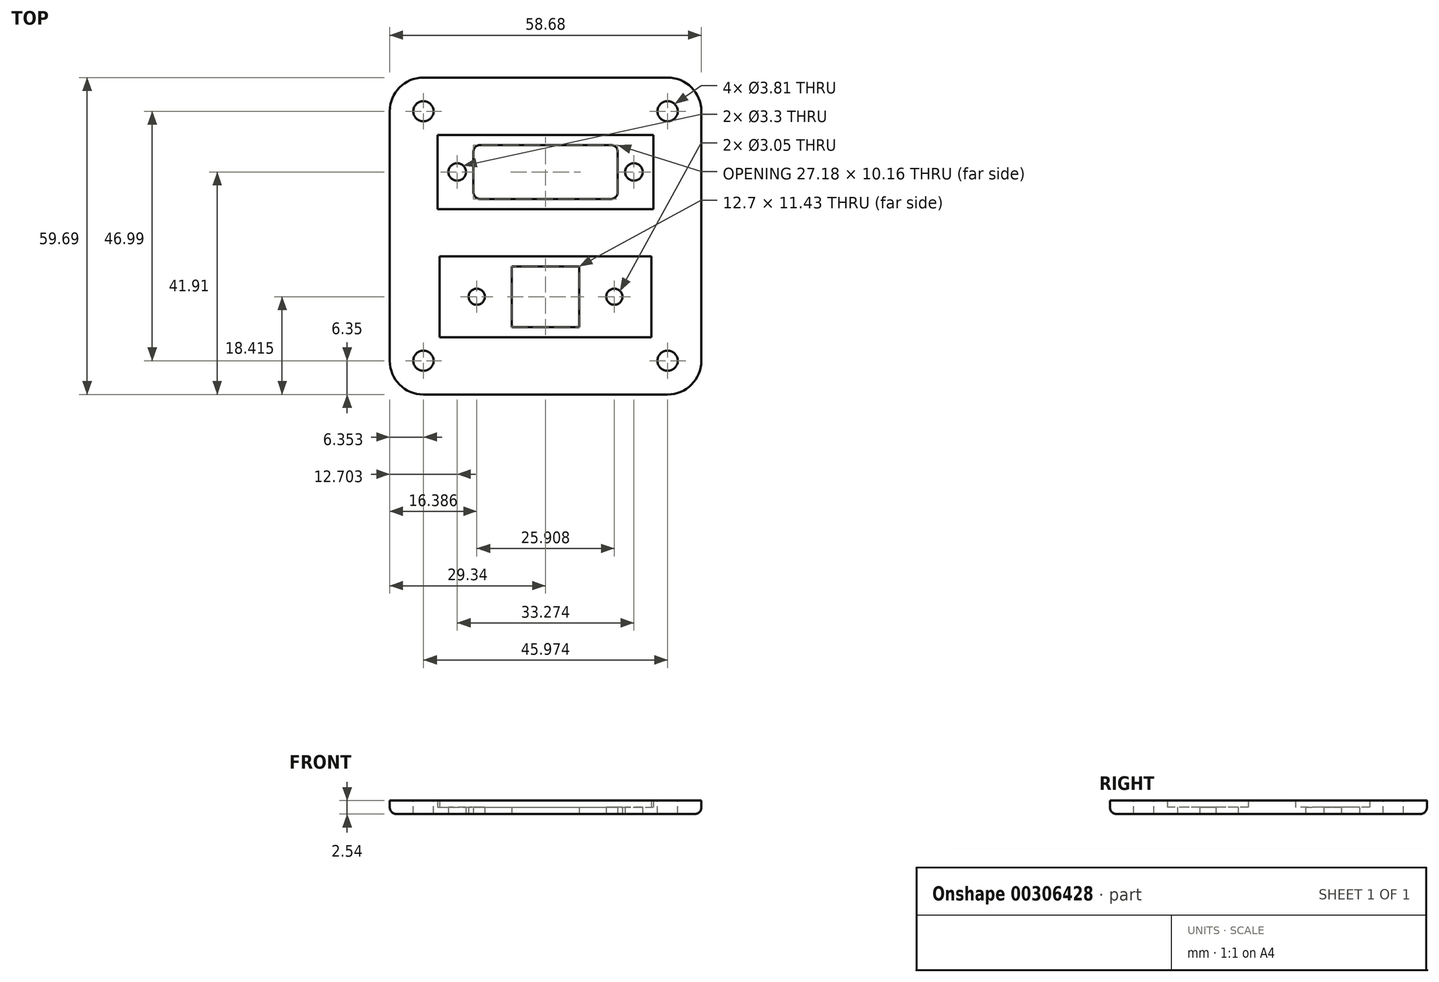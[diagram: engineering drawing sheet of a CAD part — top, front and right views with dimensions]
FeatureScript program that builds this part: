
annotation { "Feature Type Name" : "Feature", "Feature Type Description" : "" }
export const myFeature = defineFeature(function(context is Context, id is Id, definition is map)
    precondition{}
    {
        {
            var Q0;
            Q0=qCreatedBy(makeId("Top.planeOp"),FACE);
            var sketch = newSketch(context, id + "F0", { "sketchPlane" : qUnion([Q0])});
            skCircle(sketch, "E0", {"center": v(-16.64, 0) * mm, "radius": 1.65 * mm});
            skCircle(sketch, "E1", {"center": v(16.64, 0) * mm, "radius": 1.65 * mm});
            skLineSegment(sketch, "E2", {"start": v(-16.64, 0) * mm, "end": v(16.64, 0) * mm, "construction": true});
            skPoint(sketch, "E3", {"position": v(0, 0) * mm});
            skLineSegment(sketch, "E4.bottom", {"start": v(-13.59, 5.08) * mm, "end": v(13.59, 5.08) * mm});
            skLineSegment(sketch, "E4.top", {"start": v(-13.59, -5.08) * mm, "end": v(13.59, -5.08) * mm});
            skLineSegment(sketch, "E4.left", {"start": v(-13.59, 5.08) * mm, "end": v(-13.59, -5.08) * mm});
            skLineSegment(sketch, "E4.right", {"start": v(13.59, 5.08) * mm, "end": v(13.59, -5.08) * mm});
            skLineSegment(sketch, "E5.bottom", {"start": v(-6.35, -17.78) * mm, "end": v(6.35, -17.78) * mm});
            skLineSegment(sketch, "E5.top", {"start": v(-6.35, -29.21) * mm, "end": v(6.35, -29.21) * mm});
            skLineSegment(sketch, "E5.left", {"start": v(-6.35, -17.78) * mm, "end": v(-6.35, -29.21) * mm});
            skLineSegment(sketch, "E5.right", {"start": v(6.35, -17.78) * mm, "end": v(6.35, -29.21) * mm});
            skPoint(sketch, "E5.middle", {"position": v(0, -23.5) * mm});
            skCircle(sketch, "E6", {"center": v(-12.95, -23.5) * mm, "radius": 1.52 * mm});
            skCircle(sketch, "E7", {"center": v(12.95, -23.5) * mm, "radius": 1.52 * mm});
            skLineSegment(sketch, "E8", {"start": v(-12.95, -23.5) * mm, "end": v(12.95, -23.5) * mm, "construction": true});
            skLineSegment(sketch, "E9.bottom", {"start": v(-29.34, 17.78) * mm, "end": v(29.34, 17.78) * mm});
            skLineSegment(sketch, "E9.top", {"start": v(-29.34, -41.91) * mm, "end": v(29.34, -41.91) * mm});
            skLineSegment(sketch, "E9.left", {"start": v(-29.34, 17.78) * mm, "end": v(-29.34, -41.91) * mm});
            skLineSegment(sketch, "E9.right", {"start": v(29.34, 17.78) * mm, "end": v(29.34, -41.9) * mm});
            skLineSegment(sketch, "E10", {"start": v(-13.59, 5.08) * mm, "end": v(-13.59, 17.78) * mm, "construction": true});
            skLineSegment(sketch, "E11", {"start": v(6.35, -29.21) * mm, "end": v(6.35, -41.91) * mm, "construction": true});
            skLineSegment(sketch, "E12", {"start": v(-16.64, 0) * mm, "end": v(-29.34, 0) * mm, "construction": true});
            skPoint(sketch, "E13", {"position": v(0, 17.78) * mm});
            skSolve(sketch);
        }
        {
            var Q0;
            Q0 = qSketchRegion(id + "F0", true);
            extrude(context, id + "F1", {"entities" : qUnion([Q0]), "depth" : 1.27 * mm});
        }
        {
            var Q0;
            Q0=makeQuery(id+"F1.opExtrude","CAP_FACE",FACE,{"disambiguationData":[OSD([sQuery(id+"F0.wireOp",EDGE,"E0"),sQuery(id+"F0.wireOp",EDGE,"E1"),sQuery(id+"F0.wireOp",EDGE,"E4.bottom"),sQuery(id+"F0.wireOp",EDGE,"E4.top"),sQuery(id+"F0.wireOp",EDGE,"E4.left"),sQuery(id+"F0.wireOp",EDGE,"E4.right"),sQuery(id+"F0.wireOp",EDGE,"E5.bottom"),sQuery(id+"F0.wireOp",EDGE,"E5.top"),sQuery(id+"F0.wireOp",EDGE,"E5.left"),sQuery(id+"F0.wireOp",EDGE,"E5.right"),sQuery(id+"F0.wireOp",EDGE,"E6"),sQuery(id+"F0.wireOp",EDGE,"E7"),sQuery(id+"F0.wireOp",EDGE,"E9.bottom"),sQuery(id+"F0.wireOp",EDGE,"E9.top"),sQuery(id+"F0.wireOp",EDGE,"E9.left"),sQuery(id+"F0.wireOp",EDGE,"E9.right")])],"isStart":false});
            var sketch = newSketch(context, id + "F2", { "sketchPlane" : qUnion([Q0])});
            skLineSegment(sketch, "E14.bottom", {"start": v(-20.32, 6.99) * mm, "end": v(20.32, 6.99) * mm});
            skLineSegment(sketch, "E14.top", {"start": v(-20.32, -6.99) * mm, "end": v(20.32, -6.99) * mm});
            skLineSegment(sketch, "E14.left", {"start": v(-20.32, 6.99) * mm, "end": v(-20.32, -6.99) * mm});
            skLineSegment(sketch, "E14.right", {"start": v(20.32, 6.99) * mm, "end": v(20.32, -6.99) * mm});
            skPoint(sketch, "E14.middle", {"position": v(0, 0) * mm});
            skLineSegment(sketch, "E15.bottom", {"start": v(-29.34, 17.78) * mm, "end": v(29.34, 17.78) * mm});
            skLineSegment(sketch, "E15.top", {"start": v(-29.34, -41.9) * mm, "end": v(29.34, -41.9) * mm});
            skLineSegment(sketch, "E15.left", {"start": v(-29.34, 17.78) * mm, "end": v(-29.34, -41.91) * mm});
            skLineSegment(sketch, "E15.right", {"start": v(29.34, 17.78) * mm, "end": v(29.34, -41.9) * mm});
            skLineSegment(sketch, "E16.bottom", {"start": v(-19.94, -15.88) * mm, "end": v(19.94, -15.88) * mm});
            skLineSegment(sketch, "E16.top", {"start": v(-19.94, -31.12) * mm, "end": v(19.94, -31.12) * mm});
            skLineSegment(sketch, "E16.left", {"start": v(-19.94, -15.88) * mm, "end": v(-19.94, -31.12) * mm});
            skLineSegment(sketch, "E16.right", {"start": v(19.94, -15.88) * mm, "end": v(19.94, -31.12) * mm});
            skPoint(sketch, "E16.middle", {"position": v(0, -23.5) * mm});
            skPoint(sketch, "E16.middle.positionSnap0", {"position": v(0, -29.21) * mm});
            skPoint(sketch, "E16.centerSnap0", {"position": v(0, -29.21) * mm});
            skSolve(sketch);
        }
        {
            var Q0;
            Q0 = qSketchRegion(id + "F2", true);
            extrude(context, id + "F3", {"entities" : qUnion([Q0]), "operationType" : NewBodyOperationType.ADD, "depth" : 1.27 * mm});
        }
        {
            var Q0;
            Q0=makeQuery(id+"F3.boolean.opBoolean","MERGE",EDGE,{"derivedFrom":[makeQuery(id+"F1.opExtrude","SWEPT_EDGE",EDGE,{"disambiguationData":[OSD([sQuery(id+"F0.wireOp",EDGE,"E9.top"),sQuery(id+"F0.wireOp",EDGE,"E9.left")])]}),makeQuery(id+"F3.opExtrude","SWEPT_EDGE",EDGE,{"disambiguationData":[OSD([sQuery(id+"F2.wireOp",EDGE,"E15.top"),sQuery(id+"F2.wireOp",EDGE,"E15.left")])]})]});
            var Q1;
            Q1=makeQuery(id+"F3.boolean.opBoolean","MERGE",EDGE,{"derivedFrom":[makeQuery(id+"F1.opExtrude","SWEPT_EDGE",EDGE,{"disambiguationData":[OSD([sQuery(id+"F0.wireOp",EDGE,"E9.bottom"),sQuery(id+"F0.wireOp",EDGE,"E9.right")])]}),makeQuery(id+"F3.opExtrude","SWEPT_EDGE",EDGE,{"disambiguationData":[OSD([sQuery(id+"F2.wireOp",EDGE,"E15.bottom"),sQuery(id+"F2.wireOp",EDGE,"E15.right")])]})]});
            var Q2;
            Q2=makeQuery(id+"F3.boolean.opBoolean","MERGE",EDGE,{"derivedFrom":[makeQuery(id+"F1.opExtrude","SWEPT_EDGE",EDGE,{"disambiguationData":[OSD([sQuery(id+"F0.wireOp",EDGE,"E9.top"),sQuery(id+"F0.wireOp",EDGE,"E9.right")])]}),makeQuery(id+"F3.opExtrude","SWEPT_EDGE",EDGE,{"disambiguationData":[OSD([sQuery(id+"F2.wireOp",EDGE,"E15.top"),sQuery(id+"F2.wireOp",EDGE,"E15.right")])]})]});
            var Q3;
            Q3=makeQuery(id+"F3.boolean.opBoolean","MERGE",EDGE,{"derivedFrom":[makeQuery(id+"F1.opExtrude","SWEPT_EDGE",EDGE,{"disambiguationData":[OSD([sQuery(id+"F0.wireOp",EDGE,"E9.bottom"),sQuery(id+"F0.wireOp",EDGE,"E9.left")])]}),makeQuery(id+"F3.opExtrude","SWEPT_EDGE",EDGE,{"disambiguationData":[OSD([sQuery(id+"F2.wireOp",EDGE,"E15.bottom"),sQuery(id+"F2.wireOp",EDGE,"E15.left")])]})]});
            fillet(context, id + "F4", {"entities" : qUnion([Q0, Q1, Q2, Q3]), "radius" : 6.35 * mm, "tangentPropagation" : true, "allowEdgeOverflow" : false});
        }
        {
            var Q0;
            {var subQ0=sQuery(id+"F0.wireOp",EDGE,"E9.left");var subQ1=sQuery(id+"F0.wireOp",EDGE,"E9.top");Q0=makeQuery(id+"F4.opFillet","BLEND_EDGE",EDGE,{"blendedFrom":[makeQuery(id+"F3.boolean.opBoolean","MERGE",EDGE,{"derivedFrom":[makeQuery(id+"F1.opExtrude","SWEPT_EDGE",EDGE,{"disambiguationData":[OSD([subQ1,subQ0])]}),makeQuery(id+"F3.opExtrude","SWEPT_EDGE",EDGE,{"disambiguationData":[OSD([sQuery(id+"F2.wireOp",EDGE,"E15.top"),sQuery(id+"F2.wireOp",EDGE,"E15.left")])]})]}),makeQuery(id+"F1.opExtrude","CAP_FACE",FACE,{"disambiguationData":[OSD([sQuery(id+"F0.wireOp",EDGE,"E0"),sQuery(id+"F0.wireOp",EDGE,"E1"),sQuery(id+"F0.wireOp",EDGE,"E4.bottom"),sQuery(id+"F0.wireOp",EDGE,"E4.top"),sQuery(id+"F0.wireOp",EDGE,"E4.left"),sQuery(id+"F0.wireOp",EDGE,"E4.right"),sQuery(id+"F0.wireOp",EDGE,"E5.bottom"),sQuery(id+"F0.wireOp",EDGE,"E5.top"),sQuery(id+"F0.wireOp",EDGE,"E5.left"),sQuery(id+"F0.wireOp",EDGE,"E5.right"),sQuery(id+"F0.wireOp",EDGE,"E6"),sQuery(id+"F0.wireOp",EDGE,"E7"),sQuery(id+"F0.wireOp",EDGE,"E9.bottom"),subQ1,subQ0,sQuery(id+"F0.wireOp",EDGE,"E9.right")])],"isStart":true})],"blendedInto":[makeQuery(id+"F1.opExtrude","CAP_FACE",FACE,{"disambiguationData":[OSD([sQuery(id+"F0.wireOp",EDGE,"E0"),sQuery(id+"F0.wireOp",EDGE,"E1"),sQuery(id+"F0.wireOp",EDGE,"E4.bottom"),sQuery(id+"F0.wireOp",EDGE,"E4.top"),sQuery(id+"F0.wireOp",EDGE,"E4.left"),sQuery(id+"F0.wireOp",EDGE,"E4.right"),sQuery(id+"F0.wireOp",EDGE,"E5.bottom"),sQuery(id+"F0.wireOp",EDGE,"E5.top"),sQuery(id+"F0.wireOp",EDGE,"E5.left"),sQuery(id+"F0.wireOp",EDGE,"E5.right"),sQuery(id+"F0.wireOp",EDGE,"E6"),sQuery(id+"F0.wireOp",EDGE,"E7"),sQuery(id+"F0.wireOp",EDGE,"E9.bottom"),subQ1,subQ0,sQuery(id+"F0.wireOp",EDGE,"E9.right")])],"isStart":true})]});}
            var Q1;
            Q1=makeQuery(id+"F1.opExtrude","SWEPT_EDGE",EDGE,{"disambiguationData":[OSD([sQuery(id+"F0.wireOp",EDGE,"E4.bottom"),sQuery(id+"F0.wireOp",EDGE,"E4.left")])]});
            var Q2;
            Q2=makeQuery(id+"F1.opExtrude","SWEPT_EDGE",EDGE,{"disambiguationData":[OSD([sQuery(id+"F0.wireOp",EDGE,"E4.top"),sQuery(id+"F0.wireOp",EDGE,"E4.left")])]});
            var Q3;
            Q3=makeQuery(id+"F1.opExtrude","SWEPT_EDGE",EDGE,{"disambiguationData":[OSD([sQuery(id+"F0.wireOp",EDGE,"E4.top"),sQuery(id+"F0.wireOp",EDGE,"E4.right")])]});
            var Q4;
            Q4=makeQuery(id+"F1.opExtrude","SWEPT_EDGE",EDGE,{"disambiguationData":[OSD([sQuery(id+"F0.wireOp",EDGE,"E4.bottom"),sQuery(id+"F0.wireOp",EDGE,"E4.right")])]});
            fillet(context, id + "F5", {"entities" : qUnion([Q0, Q1, Q2, Q3, Q4]), "radius" : 1.27 * mm, "tangentPropagation" : true, "allowEdgeOverflow" : false});
        }
        {
            var Q0;
            Q0=makeQuery(id+"F3.opExtrude","CAP_FACE",FACE,{"disambiguationData":[OSD([sQuery(id+"F2.wireOp",EDGE,"E14.bottom"),sQuery(id+"F2.wireOp",EDGE,"E14.top"),sQuery(id+"F2.wireOp",EDGE,"E14.left"),sQuery(id+"F2.wireOp",EDGE,"E14.right"),sQuery(id+"F2.wireOp",EDGE,"E15.bottom"),sQuery(id+"F2.wireOp",EDGE,"E15.top"),sQuery(id+"F2.wireOp",EDGE,"E15.left"),sQuery(id+"F2.wireOp",EDGE,"E15.right"),sQuery(id+"F2.wireOp",EDGE,"E16.bottom"),sQuery(id+"F2.wireOp",EDGE,"E16.top"),sQuery(id+"F2.wireOp",EDGE,"E16.left"),sQuery(id+"F2.wireOp",EDGE,"E16.right")])],"isStart":false});
            var sketch = newSketch(context, id + "F6", { "sketchPlane" : qUnion([Q0])});
            skCircle(sketch, "E17", {"center": v(-22.99, 11.43) * mm, "radius": 1.9 * mm});
            skCircle(sketch, "E18", {"center": v(22.99, 11.43) * mm, "radius": 1.9 * mm});
            skCircle(sketch, "E19", {"center": v(22.99, -35.56) * mm, "radius": 1.9 * mm});
            skCircle(sketch, "E20", {"center": v(-22.99, -35.56) * mm, "radius": 1.9 * mm});
            skSolve(sketch);
        }
        {
            var Q0;
            Q0 = qSketchRegion(id + "F6", true);
            var Q1;
            Q1=makeQuery(id+"F1.opExtrude","CAP_FACE",FACE,{"disambiguationData":[OSD([sQuery(id+"F0.wireOp",EDGE,"E0"),sQuery(id+"F0.wireOp",EDGE,"E1"),sQuery(id+"F0.wireOp",EDGE,"E4.bottom"),sQuery(id+"F0.wireOp",EDGE,"E4.top"),sQuery(id+"F0.wireOp",EDGE,"E4.left"),sQuery(id+"F0.wireOp",EDGE,"E4.right"),sQuery(id+"F0.wireOp",EDGE,"E5.bottom"),sQuery(id+"F0.wireOp",EDGE,"E5.top"),sQuery(id+"F0.wireOp",EDGE,"E5.left"),sQuery(id+"F0.wireOp",EDGE,"E5.right"),sQuery(id+"F0.wireOp",EDGE,"E6"),sQuery(id+"F0.wireOp",EDGE,"E7"),sQuery(id+"F0.wireOp",EDGE,"E9.bottom"),sQuery(id+"F0.wireOp",EDGE,"E9.top"),sQuery(id+"F0.wireOp",EDGE,"E9.left"),sQuery(id+"F0.wireOp",EDGE,"E9.right")])],"isStart":true});
            extrude(context, id + "F7", {"entities" : qUnion([Q0]), "operationType" : NewBodyOperationType.REMOVE, "endBound" : BoundingType.UP_TO_SURFACE, "oppositeDirection" : true, "endBoundEntityFace" : qUnion([Q1]), "depth" : 25.4 * mm});
        }
    });
